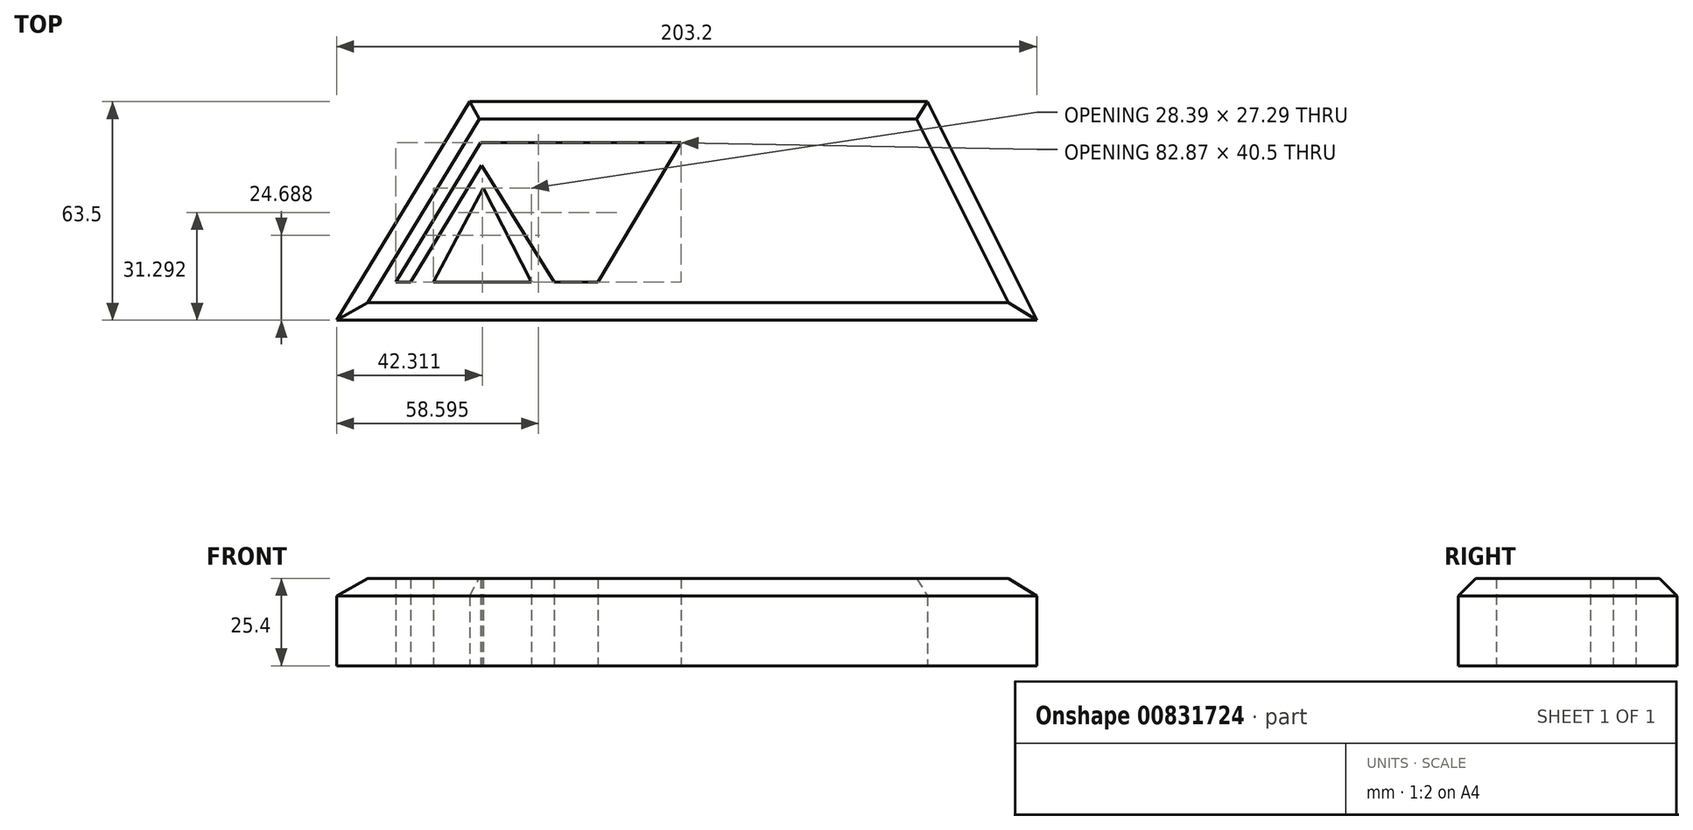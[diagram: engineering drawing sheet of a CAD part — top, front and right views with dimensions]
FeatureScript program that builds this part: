
annotation { "Feature Type Name" : "Feature", "Feature Type Description" : "" }
export const myFeature = defineFeature(function(context is Context, id is Id, definition is map)
    precondition{}
    {
        {
            var Q0;
            Q0=qCreatedBy(makeId("Top.planeOp"),FACE);
            var sketch = newSketch(context, id + "F0", { "sketchPlane" : qUnion([Q0])});
            skLineSegment(sketch, "E0", {"start": v(-135.16, 19.2) * mm, "end": v(68.04, 19.2) * mm});
            skLineSegment(sketch, "E1", {"start": v(68.04, 19.2) * mm, "end": v(36.31, 82.7) * mm});
            skLineSegment(sketch, "E2", {"start": v(36.31, 82.7) * mm, "end": v(-96.55, 82.7) * mm});
            skLineSegment(sketch, "E3", {"start": v(-96.55, 82.7) * mm, "end": v(-135.16, 19.2) * mm});
            skLineSegment(sketch, "E4", {"start": v(-93.05, 64.14) * mm, "end": v(-113.66, 30.24) * mm});
            skLineSegment(sketch, "E5", {"start": v(-113.66, 30.24) * mm, "end": v(-72.05, 30.24) * mm});
            skLineSegment(sketch, "E6", {"start": v(-93.05, 64.14) * mm, "end": v(-72.05, 30.24) * mm});
            skLineSegment(sketch, "E7", {"start": v(-107.04, 30.24) * mm, "end": v(-92.57, 57.54) * mm});
            skLineSegment(sketch, "E8", {"start": v(-92.57, 57.54) * mm, "end": v(-78.65, 30.24) * mm});
            skLineSegment(sketch, "E9", {"start": v(-113.66, 30.24) * mm, "end": v(-118, 30.24) * mm});
            skLineSegment(sketch, "E10", {"start": v(-118, 30.24) * mm, "end": v(-66.75, 30.24) * mm});
            skLineSegment(sketch, "E11", {"start": v(-66.75, 30.24) * mm, "end": v(-93.27, 70.74) * mm});
            skLineSegment(sketch, "E12", {"start": v(-93.27, 70.74) * mm, "end": v(-118, 30.24) * mm});
            skLineSegment(sketch, "E13", {"start": v(-66.75, 30.24) * mm, "end": v(41.87, 30.24) * mm});
            skLineSegment(sketch, "E14", {"start": v(-93.27, 70.74) * mm, "end": v(32.97, 70.74) * mm});
            skLineSegment(sketch, "E15", {"start": v(-86.1, 70.74) * mm, "end": v(-59.25, 30.24) * mm});
            skLineSegment(sketch, "E16", {"start": v(-59.25, 30.24) * mm, "end": v(-35.13, 70.74) * mm});
            skLineSegment(sketch, "E17", {"start": v(-79.7, 70.74) * mm, "end": v(-59.64, 39.5) * mm});
            skLineSegment(sketch, "E18", {"start": v(-59.64, 39.5) * mm, "end": v(-41.85, 70.74) * mm});
            skLineSegment(sketch, "E19", {"start": v(-73.08, 70.74) * mm, "end": v(-60.04, 50.18) * mm});
            skLineSegment(sketch, "E20", {"start": v(-60.04, 50.18) * mm, "end": v(-48.33, 70.74) * mm});
            skSolve(sketch);
        }
        {
            var Q0;
            Q0 = qSketchRegion(id + "F0", true);
            extrude(context, id + "F1", {"entities" : qUnion([Q0]), "depth" : 25.4 * mm, "offsetDistance" : 25.4 * mm});
        }
        {
            var Q0;
            Q0=makeQuery(id+"F1.opExtrude","CAP_EDGE",EDGE,{"disambiguationData":[OSD([sQuery(id+"F0.wireOp",EDGE,"E2")])],"isStart":false});
            var Q1;
            Q1=makeQuery(id+"F1.opExtrude","CAP_EDGE",EDGE,{"disambiguationData":[OSD([sQuery(id+"F0.wireOp",EDGE,"E3")])],"isStart":false});
            var Q2;
            Q2=makeQuery(id+"F1.opExtrude","CAP_EDGE",EDGE,{"disambiguationData":[OSD([sQuery(id+"F0.wireOp",EDGE,"E1")])],"isStart":false});
            chamfer(context, id + "F2", {"entities" : qUnion([Q0, Q1, Q2]), "width" : 5.08 * mm, "tangentPropagation" : true});
        }
        {
            var Q0;
            Q0=makeQuery(id+"F1.opExtrude","CAP_EDGE",EDGE,{"disambiguationData":[OSD([sQuery(id+"F0.wireOp",EDGE,"E0")])],"isStart":false});
            chamfer(context, id + "F3", {"entities" : qUnion([Q0]), "width" : 5.08 * mm, "tangentPropagation" : true});
        }
        {
            var Q0;
            {var subQ3=sQuery(id+"F0.wireOp",EDGE,"E4");Q0=makeQuery(id+"F0.imprint","IMPRINT",FACE,{"disambiguationData":[TD([[makeQuery(id+"F0.imprint","IMPRINT",EDGE,{"derivedFrom":subQ3}),1.0]])]});}
            extrude(context, id + "F4", {"entities" : qUnion([Q0]), "operationType" : NewBodyOperationType.ADD, "depth" : 25.4 * mm, "offsetDistance" : 25.4 * mm});
        }
    });
